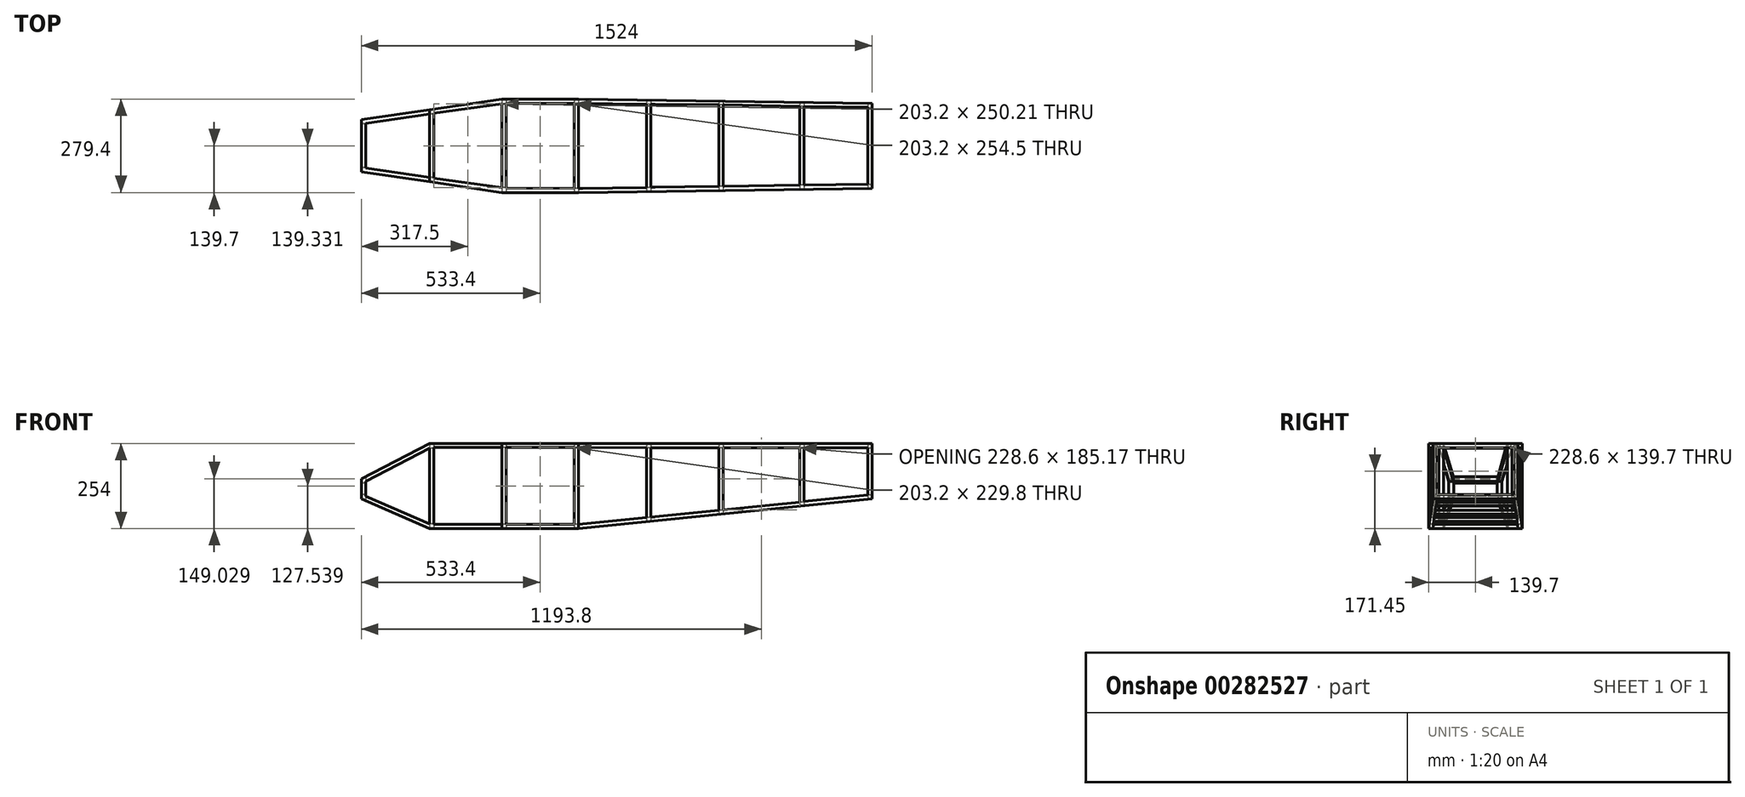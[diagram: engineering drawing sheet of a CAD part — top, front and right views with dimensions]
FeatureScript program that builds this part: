
annotation { "Feature Type Name" : "Feature", "Feature Type Description" : "" }
export const myFeature = defineFeature(function(context is Context, id is Id, definition is map)
    precondition{}
    {
        {
            var Q0;
            Q0=qCreatedBy(makeId("Top.planeOp"),FACE);
            var sketch = newSketch(context, id + "F0", { "sketchPlane" : qUnion([Q0])});
            skLineSegment(sketch, "E0.bottom", {"start": v(762, 177.8) * mm, "end": v(-762, 177.8) * mm});
            skLineSegment(sketch, "E0.top", {"start": v(762, -177.8) * mm, "end": v(-762, -177.8) * mm});
            skLineSegment(sketch, "E0.left", {"start": v(762, 177.8) * mm, "end": v(762, -177.8) * mm});
            skLineSegment(sketch, "E0.right", {"start": v(-762, 177.8) * mm, "end": v(-762, -177.8) * mm});
            skPoint(sketch, "E0.middle", {"position": v(0, 0) * mm});
            skSolve(sketch);
        }
        {
            var Q0;
            Q0=makeQuery(id+"F2.opExtrude","SWEPT_FACE",FACE,{"disambiguationData":[OSD([sQuery(id+"F0.wireOp",EDGE,"E0.top")])]});
            var sketch = newSketch(context, id + "F1", { "sketchPlane" : qUnion([Q0])});
            skLineSegment(sketch, "E1.0", {"start": v(-1003.3, -114.3) * mm, "end": v(1003.3, -114.3) * mm});
            skLineSegment(sketch, "E1.1", {"start": v(-1003.3, 114.3) * mm, "end": v(-1003.3, -114.3) * mm});
            skLineSegment(sketch, "E1.2", {"start": v(1003.3, 114.3) * mm, "end": v(-1003.3, 114.3) * mm});
            skLineSegment(sketch, "E1.3", {"start": v(1003.3, -114.3) * mm, "end": v(1003.3, 114.3) * mm});
            skSolve(sketch);
        }
        {
            var Q0;
            Q0=makeQuery(id+"F0.imprint","IMPRINT",FACE,{"disambiguationData":[TD([[makeQuery(id+"F0.imprint","IMPRINT",EDGE,{"derivedFrom":sQuery(id+"F0.wireOp",EDGE,"E0.bottom")}),1.0]])]});
            extrude(context, id + "F2", {"entities" : qUnion([Q0]), "endBound" : BoundingType.SYMMETRIC, "depth" : 254 * mm});
        }
        {
            var Q0;
            Q0=makeQuery(id+"F2.opExtrude","SWEPT_FACE",FACE,{"disambiguationData":[OSD([sQuery(id+"F0.wireOp",EDGE,"E0.left")])]});
            var sketch = newSketch(context, id + "F3", { "sketchPlane" : qUnion([Q0])});
            skLineSegment(sketch, "E2.0", {"start": v(-165.1, -114.3) * mm, "end": v(165.1, -114.3) * mm});
            skLineSegment(sketch, "E2.1", {"start": v(-165.1, 114.3) * mm, "end": v(-165.1, -114.3) * mm});
            skLineSegment(sketch, "E2.2", {"start": v(165.1, 114.3) * mm, "end": v(-165.1, 114.3) * mm});
            skLineSegment(sketch, "E2.3", {"start": v(165.1, -114.3) * mm, "end": v(165.1, 114.3) * mm});
            skSolve(sketch);
        }
        {
            var Q0;
            Q0=makeQuery(id+"F2.opExtrude","CAP_FACE",FACE,{"disambiguationData":[OSD([sQuery(id+"F0.wireOp",EDGE,"E0.bottom"),sQuery(id+"F0.wireOp",EDGE,"E0.top"),sQuery(id+"F0.wireOp",EDGE,"E0.left"),sQuery(id+"F0.wireOp",EDGE,"E0.right")])],"isStart":false});
            var sketch = newSketch(context, id + "F4", { "sketchPlane" : qUnion([Q0])});
            skLineSegment(sketch, "E3.0", {"start": v(-749.3, -165.1) * mm, "end": v(749.3, -165.1) * mm});
            skLineSegment(sketch, "E3.1", {"start": v(-749.3, 165.1) * mm, "end": v(-749.3, -165.1) * mm});
            skLineSegment(sketch, "E3.2", {"start": v(749.3, 165.1) * mm, "end": v(-749.3, 165.1) * mm});
            skLineSegment(sketch, "E3.3", {"start": v(749.3, -165.1) * mm, "end": v(749.3, 165.1) * mm});
            skSolve(sketch);
        }
        {
            var Q0;
            Q0=qCreatedBy(makeId("Front.planeOp"),FACE);
            var sketch = newSketch(context, id + "F5", { "sketchPlane" : qUnion([Q0])});
            skLineSegment(sketch, "E4.0", {"start": v(-762, 127) * mm, "end": v(-762, -127) * mm, "construction": true});
            skLineSegment(sketch, "E5.bottom", {"start": v(-558.8, -143.07) * mm, "end": v(-546.1, -143.07) * mm});
            skLineSegment(sketch, "E5.top", {"start": v(-558.8, 152.62) * mm, "end": v(-546.1, 152.62) * mm});
            skLineSegment(sketch, "E5.left", {"start": v(-558.8, -143.07) * mm, "end": v(-558.8, 152.62) * mm});
            skLineSegment(sketch, "E5.right", {"start": v(-546.1, -143.07) * mm, "end": v(-546.1, 152.62) * mm});
            skLineSegment(sketch, "E6.bottom", {"start": v(-342.9, -143.07) * mm, "end": v(-330.2, -143.07) * mm});
            skLineSegment(sketch, "E6.top", {"start": v(-342.9, 152.62) * mm, "end": v(-330.2, 152.62) * mm});
            skLineSegment(sketch, "E6.left", {"start": v(-342.9, -143.07) * mm, "end": v(-342.9, 152.62) * mm});
            skLineSegment(sketch, "E6.right", {"start": v(-330.2, -143.07) * mm, "end": v(-330.2, 152.62) * mm});
            skLineSegment(sketch, "E7.bottom", {"start": v(-127, -143.07) * mm, "end": v(-114.3, -143.07) * mm});
            skLineSegment(sketch, "E7.top", {"start": v(-127, 152.62) * mm, "end": v(-114.3, 152.62) * mm});
            skLineSegment(sketch, "E7.left", {"start": v(-127, -143.07) * mm, "end": v(-127, 152.62) * mm});
            skLineSegment(sketch, "E7.right", {"start": v(-114.3, -143.07) * mm, "end": v(-114.3, 152.62) * mm});
            skLineSegment(sketch, "E8.bottom", {"start": v(88.9, -143.07) * mm, "end": v(101.6, -143.07) * mm});
            skLineSegment(sketch, "E8.top", {"start": v(88.9, 152.62) * mm, "end": v(101.6, 152.62) * mm});
            skLineSegment(sketch, "E8.left", {"start": v(88.9, -143.07) * mm, "end": v(88.9, 152.62) * mm});
            skLineSegment(sketch, "E8.right", {"start": v(101.6, -143.07) * mm, "end": v(101.6, 152.62) * mm});
            skLineSegment(sketch, "E9", {"start": v(1356.57, 152.62) * mm, "end": v(-852.45, 152.62) * mm, "construction": true});
            skLineSegment(sketch, "E10", {"start": v(1396.25, -143.07) * mm, "end": v(-846.12, -143.07) * mm, "construction": true});
            skLineSegment(sketch, "E11.bottom", {"start": v(254, 152.62) * mm, "end": v(266.7, 152.62) * mm});
            skLineSegment(sketch, "E11.top", {"start": v(254, -143.07) * mm, "end": v(266.7, -143.07) * mm});
            skLineSegment(sketch, "E12.bottom", {"start": v(546.1, -143.07) * mm, "end": v(558.8, -143.07) * mm});
            skLineSegment(sketch, "E12.top", {"start": v(546.1, 152.62) * mm, "end": v(558.8, 152.62) * mm});
            skLineSegment(sketch, "E12.left", {"start": v(546.1, -143.07) * mm, "end": v(546.1, 152.62) * mm});
            skLineSegment(sketch, "E12.right", {"start": v(558.8, -143.07) * mm, "end": v(558.8, 152.62) * mm});
            skLineSegment(sketch, "E13.bottom", {"start": v(304.8, 152.62) * mm, "end": v(317.5, 152.62) * mm});
            skLineSegment(sketch, "E13.top", {"start": v(304.8, -143.07) * mm, "end": v(317.5, -143.07) * mm});
            skLineSegment(sketch, "E13.left", {"start": v(304.8, 152.62) * mm, "end": v(304.8, -143.07) * mm});
            skLineSegment(sketch, "E13.right", {"start": v(317.5, 152.62) * mm, "end": v(317.5, -143.07) * mm});
            skSolve(sketch);
        }
        {
            var Q0;
            Q0=qSketchRegion(id+"F5",true);
            extrude(context, id + "F6", {"entities" : qUnion([Q0]), "operationType" : NewBodyOperationType.ADD, "endBound" : BoundingType.SYMMETRIC, "depth" : 355.6 * mm});
        }
        {
            var Q0;
            Q0=qCreatedBy(makeId("Front.planeOp"),FACE);
            var sketch = newSketch(context, id + "F7", { "sketchPlane" : qUnion([Q0])});
            skLineSegment(sketch, "E14", {"start": v(-843.43, -20.57) * mm, "end": v(-558.8, 127) * mm});
            skLineSegment(sketch, "E15", {"start": v(-558.8, 127) * mm, "end": v(-1015.01, 307.35) * mm});
            skLineSegment(sketch, "E16", {"start": v(-1015.01, 307.35) * mm, "end": v(-843.43, -20.57) * mm});
            skLineSegment(sketch, "E17.0", {"start": v(-762, 127) * mm, "end": v(-762, -127) * mm, "construction": true});
            skLineSegment(sketch, "E18.0", {"start": v(762, 127) * mm, "end": v(762, -127) * mm, "construction": true});
            skLineSegment(sketch, "E19", {"start": v(-762, -38.1) * mm, "end": v(-558.8, -127) * mm});
            skLineSegment(sketch, "E20", {"start": v(-114.3, -127) * mm, "end": v(762, -38.1) * mm});
            skLineSegment(sketch, "E21", {"start": v(-762, -38.1) * mm, "end": v(-810.44, -38.1) * mm});
            skLineSegment(sketch, "E22", {"start": v(-810.44, -38.1) * mm, "end": v(-810.44, -218.05) * mm});
            skLineSegment(sketch, "E23", {"start": v(-810.44, -218.05) * mm, "end": v(819.71, -218.05) * mm});
            skLineSegment(sketch, "E24", {"start": v(819.71, -218.05) * mm, "end": v(819.71, -38.1) * mm});
            skLineSegment(sketch, "E25", {"start": v(819.71, -38.1) * mm, "end": v(762, -38.1) * mm});
            skLineSegment(sketch, "E26", {"start": v(-114.3, -127) * mm, "end": v(-558.8, -127) * mm});
            skSolve(sketch);
        }
        {
            var Q0;
            Q0=makeQuery(id+"F7.imprint","IMPRINT",FACE,{"disambiguationData":[TD([[makeQuery(id+"F7.imprint","IMPRINT",EDGE,{"derivedFrom":sQuery(id+"F7.wireOp",EDGE,"aae6dbfc-d4bc-4c02-a432-3037b792f5ca")}),1.0]])]});
            var Q1;
            Q1=makeQuery(id+"F7.imprint","IMPRINT",FACE,{"disambiguationData":[TD([[makeQuery(id+"F7.imprint","IMPRINT",EDGE,{"derivedFrom":sQuery(id+"F7.wireOp",EDGE,"E14")}),1.0]])]});
            var Q2;
            Q2=makeQuery(id+"F7.imprint","IMPRINT",FACE,{"disambiguationData":[TD([[makeQuery(id+"F7.imprint","IMPRINT",EDGE,{"derivedFrom":sQuery(id+"F7.wireOp",EDGE,"E19")}),-1.0]])]});
            extrude(context, id + "F8", {"entities" : qUnion([Q0, Q1, Q2]), "operationType" : NewBodyOperationType.REMOVE, "endBound" : BoundingType.SYMMETRIC, "oppositeDirection" : true, "depth" : 381 * mm});
        }
        {
            var Q0;
            Q0=qCreatedBy(makeId("Top.planeOp"),FACE);
            var sketch = newSketch(context, id + "F9", { "sketchPlane" : qUnion([Q0])});
            skLineSegment(sketch, "E27", {"start": v(-925.1, 0) * mm, "end": v(877.17, 0) * mm, "construction": true});
            skLineSegment(sketch, "E28", {"start": v(-885.68, 127) * mm, "end": v(840.74, 127) * mm, "construction": true});
            skLineSegment(sketch, "E29.0", {"start": v(-762, -177.8) * mm, "end": v(-762, 177.8) * mm, "construction": true});
            skLineSegment(sketch, "E30.0", {"start": v(762, 177.8) * mm, "end": v(762, -177.8) * mm, "construction": true});
            skLineSegment(sketch, "E31.0", {"start": v(-342.9, -406.4) * mm, "end": v(-342.9, -127) * mm, "construction": true});
            skLineSegment(sketch, "E32.0", {"start": v(101.6, -177.8) * mm, "end": v(101.6, 177.8) * mm, "construction": true});
            skLineSegment(sketch, "E33", {"start": v(762, 0) * mm, "end": v(762, 127) * mm});
            skLineSegment(sketch, "E34.0", {"start": v(-114.3, -177.8) * mm, "end": v(-114.3, 177.8) * mm, "construction": true});
            skLineSegment(sketch, "E35", {"start": v(-762, 77.57) * mm, "end": v(-762, 0) * mm});
            skLineSegment(sketch, "E36", {"start": v(-762, 0) * mm, "end": v(-762, 0) * mm});
            skLineSegment(sketch, "E37.MirrorCS", {"start": v(762, 0) * mm, "end": v(762, -127) * mm});
            skLineSegment(sketch, "E38.MirrorCS", {"start": v(-762, -77.57) * mm, "end": v(-762, 0) * mm});
            skLineSegment(sketch, "E39.MirrorCS", {"start": v(-885.68, -127) * mm, "end": v(840.74, -127) * mm, "construction": true});
            skLineSegment(sketch, "E40.MirrorCS", {"start": v(-762, 177.8) * mm, "end": v(-762, -177.8) * mm, "construction": true});
            skLineSegment(sketch, "E41.MirrorCS", {"start": v(762, -177.8) * mm, "end": v(762, 177.8) * mm, "construction": true});
            skLineSegment(sketch, "E42.MirrorCS", {"start": v(-342.9, 406.4) * mm, "end": v(-342.9, 127) * mm, "construction": true});
            skLineSegment(sketch, "E43.MirrorCS", {"start": v(-114.3, 177.8) * mm, "end": v(-114.3, -177.8) * mm, "construction": true});
            skLineSegment(sketch, "E44.MirrorCS", {"start": v(101.6, 177.8) * mm, "end": v(101.6, -177.8) * mm, "construction": true});
            skLineSegment(sketch, "E45.bottom", {"start": v(-858.41, 245.19) * mm, "end": v(858.29, 245.19) * mm});
            skLineSegment(sketch, "E45.top", {"start": v(-858.41, -226.45) * mm, "end": v(858.29, -226.45) * mm});
            skLineSegment(sketch, "E45.left", {"start": v(-858.41, 245.19) * mm, "end": v(-858.41, -226.45) * mm});
            skLineSegment(sketch, "E45.right", {"start": v(858.29, 245.19) * mm, "end": v(858.29, -226.45) * mm});
            skLineSegment(sketch, "E46", {"start": v(-342.9, 139.7) * mm, "end": v(-114.3, 139.7) * mm});
            skLineSegment(sketch, "E47.MirrorCS", {"start": v(-342.9, -139.7) * mm, "end": v(-114.3, -139.7) * mm});
            skLineSegment(sketch, "E48", {"start": v(-342.9, 139.7) * mm, "end": v(-762, 77.57) * mm});
            skLineSegment(sketch, "E49", {"start": v(-114.3, 139.7) * mm, "end": v(762, 127) * mm});
            skLineSegment(sketch, "E50", {"start": v(-342.9, -139.7) * mm, "end": v(-762, -77.57) * mm});
            skLineSegment(sketch, "E51", {"start": v(-114.3, -139.7) * mm, "end": v(762, -127) * mm});
            skSolve(sketch);
        }
        {
            var Q0;
            Q0=qSketchRegion(id+"F9",true);
            extrude(context, id + "F10", {"entities" : qUnion([Q0]), "operationType" : NewBodyOperationType.REMOVE, "endBound" : BoundingType.SYMMETRIC, "oppositeDirection" : true, "depth" : 381 * mm});
        }
        {
            var Q0;
            Q0=qCreatedBy(makeId("Top.planeOp"),FACE);
            var sketch = newSketch(context, id + "F11", { "sketchPlane" : qUnion([Q0])});
            skLineSegment(sketch, "E52.1", {"start": v(-749.29, -66.62) * mm, "end": v(-749.29, 66.82) * mm});
            skLineSegment(sketch, "E53.1", {"start": v(749.3, 114.99) * mm, "end": v(749.3, -114.99) * mm});
            skLineSegment(sketch, "E54.0", {"start": v(-127, 126.4) * mm, "end": v(-330.2, 126.88) * mm});
            skLineSegment(sketch, "E55.0", {"start": v(-330.2, -126.88) * mm, "end": v(-127, -127.62) * mm});
            skLineSegment(sketch, "E56.0", {"start": v(558.8, 117.24) * mm, "end": v(749.3, 114.48) * mm});
            skLineSegment(sketch, "E57.0", {"start": v(558.8, -117.24) * mm, "end": v(749.3, -114.48) * mm});
            skLineSegment(sketch, "E58.0", {"start": v(-749.29, -66.62) * mm, "end": v(-558.8, -94.86) * mm});
            skLineSegment(sketch, "E59", {"start": v(-342.9, -125.1) * mm, "end": v(-546.1, -96.69) * mm});
            skLineSegment(sketch, "E60", {"start": v(-546.1, 96.69) * mm, "end": v(-342.9, 125.1) * mm});
            skLineSegment(sketch, "E61.0.1", {"start": v(-546.1, -96.69) * mm, "end": v(-546.1, 96.69) * mm});
            skLineSegment(sketch, "E61.0.3", {"start": v(-558.8, 94.78) * mm, "end": v(-558.8, -94.86) * mm});
            skLineSegment(sketch, "E62.0.1", {"start": v(-342.9, 125.1) * mm, "end": v(-342.9, -125.1) * mm});
            skLineSegment(sketch, "E63.0.1", {"start": v(88.9, 124.23) * mm, "end": v(88.9, -124.5) * mm});
            skLineSegment(sketch, "E63.0.3", {"start": v(101.6, -124.3) * mm, "end": v(101.6, 124.05) * mm});
            skLineSegment(sketch, "E64.0.1", {"start": v(304.8, 122.67) * mm, "end": v(304.8, -121.36) * mm});
            skLineSegment(sketch, "E64.0.3", {"start": v(317.5, -120.83) * mm, "end": v(317.5, 122.5) * mm});
            skLineSegment(sketch, "E65.0.1", {"start": v(546.1, 117.12) * mm, "end": v(546.1, -117.44) * mm});
            skLineSegment(sketch, "E65.0.3", {"start": v(558.8, -117.24) * mm, "end": v(558.8, 117.24) * mm});
            skLineSegment(sketch, "E66.trimOffspring", {"start": v(304.8, -121.36) * mm, "end": v(101.6, -124.3) * mm});
            skLineSegment(sketch, "E67.trimOffspring", {"start": v(88.9, -124.5) * mm, "end": v(-114.3, -127.44) * mm});
            skLineSegment(sketch, "E68.trimOffspring", {"start": v(101.6, 124.05) * mm, "end": v(304.8, 122.67) * mm});
            skPoint(sketch, "E61.0.2.end.orphan", {"position": v(-558.8, 107.7) * mm});
            skPoint(sketch, "E61.0.2.start.orphan", {"position": v(-546.1, 109.58) * mm});
            skPoint(sketch, "E69.orphan", {"position": v(-558.8, -107.7) * mm});
            skPoint(sketch, "E70.orphan", {"position": v(-546.1, -109.58) * mm});
            skLineSegment(sketch, "E71", {"start": v(-749.29, 66.82) * mm, "end": v(-558.8, 94.78) * mm});
            skLineSegment(sketch, "E72", {"start": v(-114.3, -127.44) * mm, "end": v(-114.3, 126.4) * mm});
            skLineSegment(sketch, "E73", {"start": v(-330.2, 126.88) * mm, "end": v(-330.2, -126.88) * mm});
            skLineSegment(sketch, "E74", {"start": v(-127, 126.4) * mm, "end": v(-127, -127.62) * mm});
            skLineSegment(sketch, "E75", {"start": v(546.1, -117.44) * mm, "end": v(317.5, -120.83) * mm});
            skLineSegment(sketch, "E76", {"start": v(88.9, 124.23) * mm, "end": v(-114.3, 126.4) * mm});
            skLineSegment(sketch, "E77", {"start": v(546.1, 117.12) * mm, "end": v(317.5, 122.5) * mm});
            skSolve(sketch);
        }
        {
            var Q0;
            Q0=qSketchRegion(id+"F11",true);
            extrude(context, id + "F12", {"entities" : qUnion([Q0]), "operationType" : NewBodyOperationType.REMOVE, "endBound" : BoundingType.SYMMETRIC, "depth" : 381 * mm});
        }
        {
            var Q0;
            Q0=qCreatedBy(makeId("Front.planeOp"),FACE);
            var sketch = newSketch(context, id + "F13", { "sketchPlane" : qUnion([Q0])});
            skLineSegment(sketch, "E78.0", {"start": v(-749.3, 13.93) * mm, "end": v(-558.8, 112.7) * mm});
            skLineSegment(sketch, "E78.1", {"start": v(-749.3, -29.8) * mm, "end": v(-749.3, 13.93) * mm});
            skLineSegment(sketch, "E78.2", {"start": v(-749.3, -29.8) * mm, "end": v(-558.8, -113.14) * mm});
            skLineSegment(sketch, "E78.3", {"start": v(-342.9, -114.3) * mm, "end": v(-546.1, -114.3) * mm});
            skLineSegment(sketch, "E79.0", {"start": v(749.3, -26.62) * mm, "end": v(558.8, -45.95) * mm});
            skLineSegment(sketch, "E79.1", {"start": v(749.3, -26.62) * mm, "end": v(749.3, 114.3) * mm});
            skLineSegment(sketch, "E79.2", {"start": v(558.8, 114.3) * mm, "end": v(749.3, 114.3) * mm});
            skLineSegment(sketch, "E80", {"start": v(-127, -114.36) * mm, "end": v(-330.2, -114.3) * mm});
            skLineSegment(sketch, "E81.0.1", {"start": v(558.8, 114.3) * mm, "end": v(558.8, -45.95) * mm});
            skLineSegment(sketch, "E82.0.1", {"start": v(101.6, 114.89) * mm, "end": v(101.6, -92.46) * mm});
            skLineSegment(sketch, "E82.0.3", {"start": v(304.8, -71.84) * mm, "end": v(304.8, 114.63) * mm});
            skLineSegment(sketch, "E83.0.0", {"start": v(-330.2, 115.44) * mm, "end": v(-330.2, -114.3) * mm});
            skLineSegment(sketch, "E83.0.2", {"start": v(-127, -114.36) * mm, "end": v(-127, 115.18) * mm});
            skLineSegment(sketch, "E84.0.1", {"start": v(-546.1, 115.71) * mm, "end": v(-546.1, -114.3) * mm});
            skLineSegment(sketch, "E84.0.3", {"start": v(-342.9, -114.3) * mm, "end": v(-342.9, 115.45) * mm});
            skLineSegment(sketch, "E85.0.2", {"start": v(-558.8, -113.14) * mm, "end": v(-558.8, 112.7) * mm});
            skPoint(sketch, "E81.0.0.start.orphan", {"position": v(749.3, 127) * mm});
            skPoint(sketch, "E86.orphan", {"position": v(558.8, 127) * mm});
            skPoint(sketch, "E87.0.0.start.orphan", {"position": v(558.8, 126.99) * mm});
            skLineSegment(sketch, "E88.trimOffspring", {"start": v(304.8, 114.63) * mm, "end": v(101.6, 114.89) * mm});
            skPoint(sketch, "E82.0.0.start.orphan", {"position": v(304.8, 127) * mm});
            skLineSegment(sketch, "E89.trimOffspring", {"start": v(-127, 115.18) * mm, "end": v(-330.2, 115.44) * mm});
            skPoint(sketch, "E83.0.1.end.orphan", {"position": v(-127, -127) * mm});
            skPoint(sketch, "E90.orphan", {"position": v(-330.2, -127) * mm});
            skLineSegment(sketch, "E91.trimOffspring", {"start": v(-342.9, 115.45) * mm, "end": v(-546.1, 115.71) * mm});
            skPoint(sketch, "E83.0.3.end.orphan", {"position": v(-330.2, 127) * mm});
            skPoint(sketch, "E83.0.3.start.orphan", {"position": v(-127, 127) * mm});
            skPoint(sketch, "E84.0.2.end.orphan", {"position": v(-342.9, -127) * mm});
            skPoint(sketch, "E92.orphan", {"position": v(-546.1, -127) * mm});
            skPoint(sketch, "E93.orphan", {"position": v(-546.1, 127) * mm});
            skPoint(sketch, "E85.0.3.start.orphan", {"position": v(-558.8, 127) * mm});
            skPoint(sketch, "E94.orphan", {"position": v(101.6, 127) * mm});
            skLineSegment(sketch, "E95", {"start": v(546.1, -48.1) * mm, "end": v(456.3, -56.47) * mm});
            skPoint(sketch, "E81.0.2.end.orphan", {"position": v(749.3, -39.39) * mm});
            skPoint(sketch, "E96.orphan", {"position": v(-342.9, 127) * mm});
            skLineSegment(sketch, "E97.left", {"start": v(-680.76, 244.02) * mm, "end": v(-680.76, 242.67) * mm});
            skLineSegment(sketch, "E97.right", {"start": v(-640.08, 244.02) * mm, "end": v(-640.08, 242.67) * mm});
            skLineSegment(sketch, "E98.bottom", {"start": v(851.63, 270.75) * mm, "end": v(-718.73, 270.75) * mm});
            skLineSegment(sketch, "E98.top", {"start": v(851.63, 127) * mm, "end": v(-718.73, 127) * mm});
            skLineSegment(sketch, "E98.left", {"start": v(851.63, 270.75) * mm, "end": v(851.63, 127) * mm});
            skLineSegment(sketch, "E98.right", {"start": v(-718.73, 270.75) * mm, "end": v(-718.73, 127) * mm});
            skLineSegment(sketch, "E99", {"start": v(-114.3, -114.36) * mm, "end": v(88.9, -93.75) * mm});
            skLineSegment(sketch, "E100", {"start": v(546.1, 114.3) * mm, "end": v(317.5, 114.61) * mm});
            skLineSegment(sketch, "E101", {"start": v(88.9, 114.9) * mm, "end": v(-114.3, 115.18) * mm});
            skLineSegment(sketch, "E102", {"start": v(-114.3, 115.18) * mm, "end": v(-114.3, -114.36) * mm});
            skLineSegment(sketch, "E103", {"start": v(88.9, 114.9) * mm, "end": v(88.9, -93.75) * mm});
            skLineSegment(sketch, "E104", {"start": v(317.5, 114.61) * mm, "end": v(317.5, -70.55) * mm});
            skLineSegment(sketch, "E105", {"start": v(546.1, 114.3) * mm, "end": v(546.1, -48.1) * mm});
            skLineSegment(sketch, "E106.trimOffspring", {"start": v(317.5, -70.55) * mm, "end": v(456.3, -56.47) * mm});
            skLineSegment(sketch, "E107.trimOffspring", {"start": v(101.6, -92.46) * mm, "end": v(304.8, -71.84) * mm});
            skSolve(sketch);
        }
        {
            var Q0;
            Q0 = qSketchRegion(id + "F13", true);
            extrude(context, id + "F14", {"entities" : qUnion([Q0]), "operationType" : NewBodyOperationType.REMOVE, "endBound" : BoundingType.SYMMETRIC, "oppositeDirection" : true, "depth" : 381 * mm});
        }
        {
            var Q0;
            {var subQ4=sQuery(id+"F5.wireOp",EDGE,"E5.top");var subQ11=sQuery(id+"F5.wireOp",EDGE,"E5.left");Q0=makeQuery(id+"F14.boolean.opBoolean","MERGE",FACE,{"derivedFrom":[makeQuery(id+"F12.boolean.opBoolean","MERGE",FACE,{"derivedFrom":[makeQuery(id+"F6.boolean.opBoolean","SPLIT",FACE,{"disambiguationData":[TD([makeQuery(id+"F6.opExtrude","SWEPT_FACE",FACE,{"disambiguationData":[OSD([subQ4])]})])],"derivedFrom":makeQuery(id+"F6.opExtrude","SWEPT_FACE",FACE,{"disambiguationData":[OSD([subQ11])]})}),makeQuery(id+"F12.opExtrude","SWEPT_FACE",FACE,{"disambiguationData":[OSD([sQuery(id+"F11.wireOp",EDGE,"76c89935-962c-43c5-8293-adbbc792d1c5.0")])]})]}),makeQuery(id+"F14.opExtrude","SWEPT_FACE",FACE,{"disambiguationData":[OSD([sQuery(id+"F13.wireOp",EDGE,"9ef2c277-a94d-4be6-9fd4-f6ea86bf56da.0.3")])]})]});}
            var sketch = newSketch(context, id + "F15", { "sketchPlane" : qUnion([Q0])});
            skLineSegment(sketch, "E108.bottom", {"start": v(-94.78, 112.7) * mm, "end": v(94.86, 112.7) * mm});
            skLineSegment(sketch, "E108.top", {"start": v(-94.78, -113.14) * mm, "end": v(94.86, -113.14) * mm});
            skLineSegment(sketch, "E108.left", {"start": v(-94.78, 112.7) * mm, "end": v(-94.78, -113.14) * mm});
            skLineSegment(sketch, "E108.right", {"start": v(94.86, 112.7) * mm, "end": v(94.86, -113.14) * mm});
            skSolve(sketch);
        }
        {
            var Q0;
            Q0=qSketchRegion(id+"F15",true);
            extrude(context, id + "F16", {"entities" : qUnion([Q0]), "operationType" : NewBodyOperationType.REMOVE, "oppositeDirection" : true, "depth" : 25.4 * mm});
        }
        {
            var Q0;
            {var subQ1=sQuery(id+"F5.wireOp",EDGE,"E6.left");var subQ2=sQuery(id+"F5.wireOp",EDGE,"E6.top");Q0=makeQuery(id+"F14.boolean.opBoolean","MERGE",FACE,{"derivedFrom":[makeQuery(id+"F12.boolean.opBoolean","MERGE",FACE,{"derivedFrom":[makeQuery(id+"F6.boolean.opBoolean","SPLIT",FACE,{"disambiguationData":[TD([makeQuery(id+"F6.opExtrude","SWEPT_FACE",FACE,{"disambiguationData":[OSD([subQ2])]})])],"derivedFrom":makeQuery(id+"F6.opExtrude","SWEPT_FACE",FACE,{"disambiguationData":[OSD([subQ1])]})}),makeQuery(id+"F12.opExtrude","SWEPT_FACE",FACE,{"disambiguationData":[OSD([sQuery(id+"F11.wireOp",EDGE,"7b3102ac-ed15-4f5d-bc17-57cfcd7eebf1.0")])]})]}),makeQuery(id+"F14.opExtrude","SWEPT_FACE",FACE,{"disambiguationData":[OSD([sQuery(id+"F13.wireOp",EDGE,"8vpACN4d-Oada-hr1t-Xb63-NezVnV2j5PEM")])]})]});}
            var sketch = newSketch(context, id + "F17", { "sketchPlane" : qUnion([Q0])});
            skLineSegment(sketch, "E109.bottom", {"start": v(-125.1, 115.45) * mm, "end": v(125.1, 115.45) * mm});
            skLineSegment(sketch, "E109.top", {"start": v(-125.1, -114.3) * mm, "end": v(125.1, -114.3) * mm});
            skLineSegment(sketch, "E109.left", {"start": v(-125.1, 115.45) * mm, "end": v(-125.1, -114.3) * mm});
            skLineSegment(sketch, "E109.right", {"start": v(125.1, 115.45) * mm, "end": v(125.1, -114.3) * mm});
            skSolve(sketch);
        }
        {
            var Q0;
            Q0=qSketchRegion(id+"F17",true);
            extrude(context, id + "F18", {"entities" : qUnion([Q0]), "operationType" : NewBodyOperationType.REMOVE, "oppositeDirection" : true, "depth" : 25.4 * mm});
        }
        {
            var Q0;
            {var subQ8=sQuery(id+"F5.wireOp",EDGE,"E7.top");var subQ16=sQuery(id+"F5.wireOp",EDGE,"E7.left");Q0=makeQuery(id+"F14.boolean.opBoolean","MERGE",FACE,{"derivedFrom":[makeQuery(id+"F12.boolean.opBoolean","MERGE",FACE,{"derivedFrom":[makeQuery(id+"F6.boolean.opBoolean","SPLIT",FACE,{"disambiguationData":[TD([makeQuery(id+"F6.opExtrude","SWEPT_FACE",FACE,{"disambiguationData":[OSD([subQ8])]})])],"derivedFrom":makeQuery(id+"F6.opExtrude","SWEPT_FACE",FACE,{"disambiguationData":[OSD([subQ16])]})}),makeQuery(id+"F12.opExtrude","SWEPT_FACE",FACE,{"disambiguationData":[OSD([sQuery(id+"F11.wireOp",EDGE,"b35c1112-db7b-4928-a18e-9a17467dcdab.0")])]})]}),makeQuery(id+"F14.opExtrude","SWEPT_FACE",FACE,{"disambiguationData":[OSD([sQuery(id+"F13.wireOp",EDGE,"fa40cc79-636a-4cbc-a25d-f27d8fe22ac2.0.3")])]})]});}
            var sketch = newSketch(context, id + "F19", { "sketchPlane" : qUnion([Q0])});
            skLineSegment(sketch, "E110.bottom", {"start": v(-126.4, 115.18) * mm, "end": v(127.62, 115.18) * mm});
            skLineSegment(sketch, "E110.top", {"start": v(-126.4, -114.36) * mm, "end": v(127.62, -114.36) * mm});
            skLineSegment(sketch, "E110.left", {"start": v(-126.4, 115.18) * mm, "end": v(-126.4, -114.36) * mm});
            skLineSegment(sketch, "E110.right", {"start": v(127.62, 115.18) * mm, "end": v(127.62, -114.36) * mm});
            skSolve(sketch);
        }
        {
            var Q0;
            Q0=qSketchRegion(id+"F19",true);
            extrude(context, id + "F20", {"entities" : qUnion([Q0]), "operationType" : NewBodyOperationType.REMOVE, "oppositeDirection" : true, "depth" : 25.4 * mm});
        }
        {
            var Q0;
            {var subQ0=sQuery(id+"F5.wireOp",EDGE,"E8.bottom");var subQ36=sQuery(id+"F5.wireOp",EDGE,"E8.left");var subQ37=sQuery(id+"F5.wireOp",EDGE,"E8.top");var subQ60=makeQuery(id+"F6.opExtrude","SWEPT_FACE",FACE,{"disambiguationData":[OSD([subQ36])]});Q0=makeQuery(id+"F14.boolean.opBoolean","MERGE",FACE,{"derivedFrom":[makeQuery(id+"F12.boolean.opBoolean","MERGE",FACE,{"derivedFrom":[makeQuery(id+"F6.boolean.opBoolean","SPLIT",FACE,{"disambiguationData":[TD([makeQuery(id+"F6.opExtrude","SWEPT_FACE",FACE,{"disambiguationData":[OSD([subQ37])]})])],"derivedFrom":subQ60}),makeQuery(id+"F6.boolean.opBoolean","SPLIT",FACE,{"disambiguationData":[TD([makeQuery(id+"F6.opExtrude","SWEPT_FACE",FACE,{"disambiguationData":[OSD([subQ0])]})])],"derivedFrom":subQ60}),makeQuery(id+"F12.opExtrude","SWEPT_FACE",FACE,{"disambiguationData":[OSD([sQuery(id+"F11.wireOp",EDGE,"7310f20e-b108-4276-8773-8cf4f74fe12c.0")])]})]}),makeQuery(id+"F14.opExtrude","SWEPT_FACE",FACE,{"disambiguationData":[OSD([sQuery(id+"F13.wireOp",EDGE,"FrRoJ9V7-tiAn-pTb4-UzEj-WxOpO9FH2ecp")])]})]});}
            var sketch = newSketch(context, id + "F21", { "sketchPlane" : qUnion([Q0])});
            skLineSegment(sketch, "E111.bottom", {"start": v(-124.23, 114.9) * mm, "end": v(124.5, 114.9) * mm});
            skLineSegment(sketch, "E111.top", {"start": v(-124.23, -93.75) * mm, "end": v(124.5, -93.75) * mm});
            skLineSegment(sketch, "E111.left", {"start": v(-124.23, 114.9) * mm, "end": v(-124.23, -93.75) * mm});
            skLineSegment(sketch, "E111.right", {"start": v(124.5, 114.9) * mm, "end": v(124.5, -93.75) * mm});
            skSolve(sketch);
        }
        {
            var Q0;
            Q0=qSketchRegion(id+"F21",true);
            extrude(context, id + "F22", {"entities" : qUnion([Q0]), "operationType" : NewBodyOperationType.REMOVE, "oppositeDirection" : true, "depth" : 25.4 * mm});
        }
        {
            var Q0;
            {var subQ35=sQuery(id+"F5.wireOp",EDGE,"E13.left");var subQ37=sQuery(id+"F5.wireOp",EDGE,"E13.bottom");Q0=makeQuery(id+"F14.boolean.opBoolean","MERGE",FACE,{"derivedFrom":[makeQuery(id+"F12.boolean.opBoolean","MERGE",FACE,{"derivedFrom":[makeQuery(id+"F6.boolean.opBoolean","SPLIT",FACE,{"disambiguationData":[TD([makeQuery(id+"F6.opExtrude","SWEPT_FACE",FACE,{"disambiguationData":[OSD([subQ37])]})])],"derivedFrom":makeQuery(id+"F6.opExtrude","SWEPT_FACE",FACE,{"disambiguationData":[OSD([subQ35])]})}),makeQuery(id+"F12.opExtrude","SWEPT_FACE",FACE,{"disambiguationData":[OSD([sQuery(id+"F11.wireOp",EDGE,"b7ba8543-acbf-43cf-88d8-2159336d2e7e.0")])]})]}),makeQuery(id+"F14.opExtrude","SWEPT_FACE",FACE,{"disambiguationData":[OSD([sQuery(id+"F13.wireOp",EDGE,"MzW9eNza-KUkf-pAGu-OPrh-YCygVrhiN9A4")])]})]});}
            var sketch = newSketch(context, id + "F23", { "sketchPlane" : qUnion([Q0])});
            skLineSegment(sketch, "E112.bottom", {"start": v(-122.67, 114.63) * mm, "end": v(121.36, 114.63) * mm});
            skLineSegment(sketch, "E112.top", {"start": v(-122.67, -71.84) * mm, "end": v(121.36, -71.84) * mm});
            skLineSegment(sketch, "E112.left", {"start": v(-122.67, 114.63) * mm, "end": v(-122.67, -71.84) * mm});
            skLineSegment(sketch, "E112.right", {"start": v(121.36, 114.63) * mm, "end": v(121.36, -71.84) * mm});
            skSolve(sketch);
        }
        {
            var Q0;
            Q0=qSketchRegion(id+"F23",true);
            extrude(context, id + "F24", {"entities" : qUnion([Q0]), "operationType" : NewBodyOperationType.REMOVE, "oppositeDirection" : true, "depth" : 15.24 * mm});
        }
        {
            var Q0;
            {var subQ18=sQuery(id+"F5.wireOp",EDGE,"E12.left");var subQ19=sQuery(id+"F5.wireOp",EDGE,"E12.top");Q0=makeQuery(id+"F14.boolean.opBoolean","MERGE",FACE,{"derivedFrom":[makeQuery(id+"F12.boolean.opBoolean","MERGE",FACE,{"derivedFrom":[makeQuery(id+"F6.boolean.opBoolean","SPLIT",FACE,{"disambiguationData":[TD([makeQuery(id+"F6.opExtrude","SWEPT_FACE",FACE,{"disambiguationData":[OSD([subQ19])]})])],"derivedFrom":makeQuery(id+"F6.opExtrude","SWEPT_FACE",FACE,{"disambiguationData":[OSD([subQ18])]})}),makeQuery(id+"F12.opExtrude","SWEPT_FACE",FACE,{"disambiguationData":[OSD([sQuery(id+"F11.wireOp",EDGE,"94f42aec-5a63-4bb3-a17e-c23af455982a.0")])]})]}),makeQuery(id+"F14.opExtrude","SWEPT_FACE",FACE,{"disambiguationData":[OSD([sQuery(id+"F13.wireOp",EDGE,"4bo9Z2lR-88Dg-C45D-lGNA-9ZzvTnCFj7b6")])]})]});}
            var sketch = newSketch(context, id + "F25", { "sketchPlane" : qUnion([Q0])});
            skLineSegment(sketch, "E113.bottom", {"start": v(-117.12, 114.3) * mm, "end": v(117.44, 114.3) * mm});
            skLineSegment(sketch, "E113.top", {"start": v(-117.12, -48.1) * mm, "end": v(117.44, -48.1) * mm});
            skLineSegment(sketch, "E113.left", {"start": v(117.44, 114.3) * mm, "end": v(117.44, -48.1) * mm});
            skLineSegment(sketch, "E113.right", {"start": v(-117.12, 114.3) * mm, "end": v(-117.12, -48.1) * mm});
            skSolve(sketch);
        }
        {
            var Q0;
            Q0=qSketchRegion(id+"F25",true);
            extrude(context, id + "F26", {"entities" : qUnion([Q0]), "operationType" : NewBodyOperationType.REMOVE, "oppositeDirection" : true, "depth" : 13.97 * mm});
        }
        {
            var Q0;
            Q0=makeQuery(id+"F14.boolean.opBoolean","MERGE",FACE,{"derivedFrom":[makeQuery(id+"F12.boolean.opBoolean","COPY",FACE,{"derivedFrom":makeQuery(id+"F12.opExtrude","SWEPT_FACE",FACE,{"disambiguationData":[OSD([sQuery(id+"F11.wireOp",EDGE,"adecc727-4d20-49de-aa06-e82a0813468d.1")])]})}),makeQuery(id+"F14.opExtrude","SWEPT_FACE",FACE,{"disambiguationData":[OSD([sQuery(id+"F13.wireOp",EDGE,"9f7ba322-1395-4fc7-9540-b671459040af.2")])]})]});
            var sketch = newSketch(context, id + "F27", { "sketchPlane" : qUnion([Q0])});
            skLineSegment(sketch, "E114.bottom", {"start": v(-114.91, 114.3) * mm, "end": v(114.6, 114.3) * mm});
            skLineSegment(sketch, "E114.top", {"start": v(-114.91, -7.58) * mm, "end": v(114.6, -7.58) * mm});
            skLineSegment(sketch, "E114.left", {"start": v(-114.91, 114.3) * mm, "end": v(-114.91, -7.58) * mm});
            skLineSegment(sketch, "E114.right", {"start": v(114.6, 114.3) * mm, "end": v(114.6, -7.58) * mm});
            skSolve(sketch);
        }
        {
            var Q0;
            Q0=makeQuery(id+"F2.opExtrude","SWEPT_FACE",FACE,{"disambiguationData":[OSD([sQuery(id+"F0.wireOp",EDGE,"E0.right")])]});
            var sketch = newSketch(context, id + "F28", { "sketchPlane" : qUnion([Q0])});
            skLineSegment(sketch, "E115.0", {"start": v(-64.87, 8.95) * mm, "end": v(64.87, 8.95) * mm});
            skLineSegment(sketch, "E116.0", {"start": v(-64.87, -25.4) * mm, "end": v(-64.87, 8.95) * mm});
            skLineSegment(sketch, "E116.1", {"start": v(-64.87, -25.4) * mm, "end": v(64.87, -25.4) * mm});
            skLineSegment(sketch, "E116.2", {"start": v(64.87, -25.4) * mm, "end": v(64.87, 8.95) * mm});
            skSolve(sketch);
        }
        {
            var Q0;
            Q0=qSketchRegion(id+"F28",true);
            extrude(context, id + "F29", {"entities" : qUnion([Q0]), "operationType" : NewBodyOperationType.REMOVE, "oppositeDirection" : true, "depth" : 25.4 * mm});
        }
        {
            var Q0;
            Q0=makeQuery(id+"F2.opExtrude","SWEPT_FACE",FACE,{"disambiguationData":[OSD([sQuery(id+"F0.wireOp",EDGE,"E0.left")])]});
            var sketch = newSketch(context, id + "F30", { "sketchPlane" : qUnion([Q0])});
            skLineSegment(sketch, "E117.bottom", {"start": v(-114.3, 114.3) * mm, "end": v(114.3, 114.3) * mm});
            skLineSegment(sketch, "E117.top", {"start": v(-114.3, -25.4) * mm, "end": v(114.3, -25.4) * mm});
            skLineSegment(sketch, "E117.left", {"start": v(-114.3, 114.3) * mm, "end": v(-114.3, -25.4) * mm});
            skLineSegment(sketch, "E117.right", {"start": v(114.3, 114.3) * mm, "end": v(114.3, -25.4) * mm});
            skSolve(sketch);
        }
        {
            var Q0;
            Q0=makeQuery(id+"F30.imprint","IMPRINT",FACE,{"disambiguationData":[TD([[makeQuery(id+"F30.imprint","IMPRINT",EDGE,{"derivedFrom":sQuery(id+"F30.wireOp",EDGE,"E117.bottom")}),-1.0]])]});
            extrude(context, id + "F31", {"entities" : qUnion([Q0]), "operationType" : NewBodyOperationType.REMOVE, "oppositeDirection" : true, "depth" : 12.7 * mm});
        }
    });
